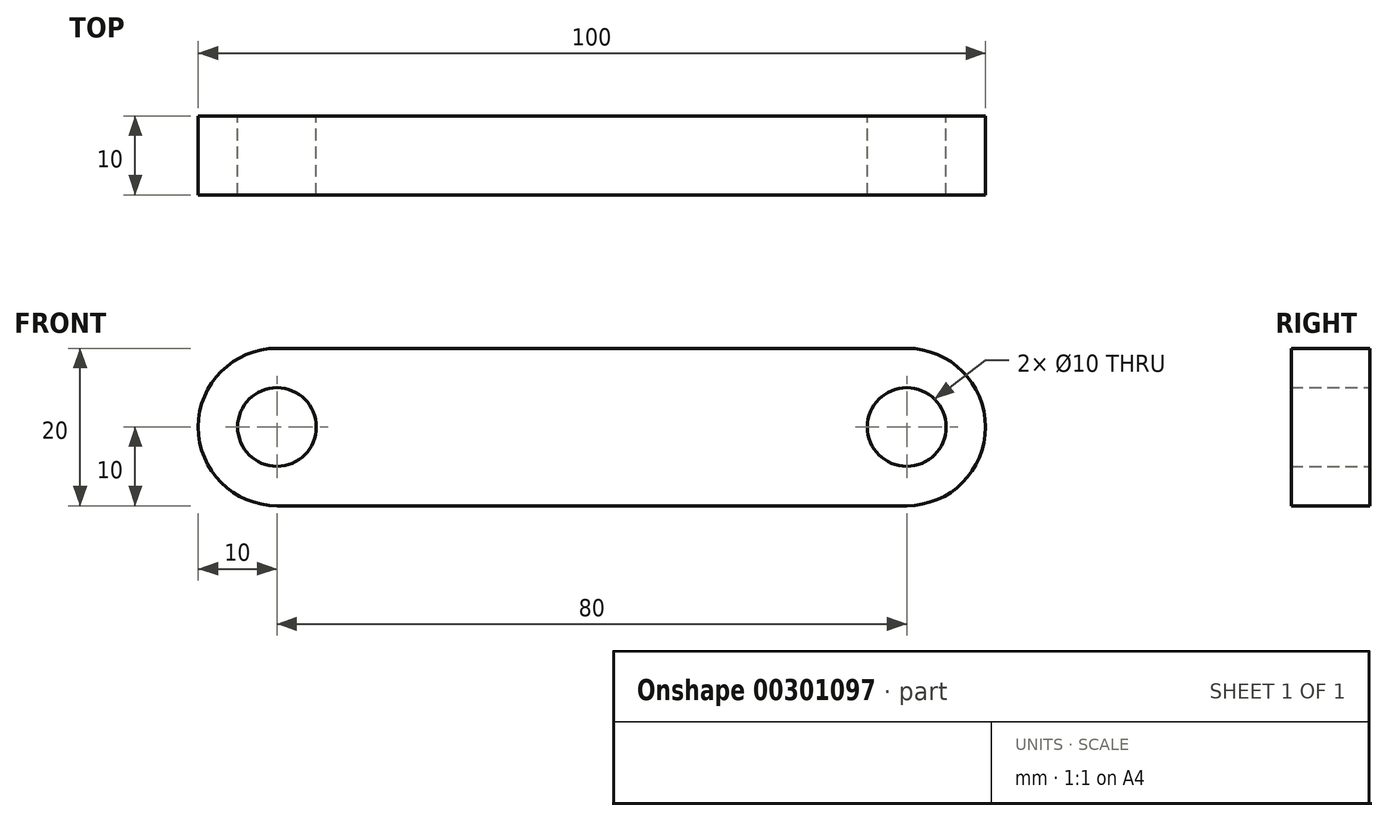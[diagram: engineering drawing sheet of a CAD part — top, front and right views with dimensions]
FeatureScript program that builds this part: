
annotation { "Feature Type Name" : "Feature", "Feature Type Description" : "" }
export const myFeature = defineFeature(function(context is Context, id is Id, definition is map)
    precondition{}
    {
        {
            var Q0;
            Q0=qCreatedBy(makeId("Front.planeOp"),FACE);
            var sketch = newSketch(context, id + "F0", { "sketchPlane" : qUnion([Q0])});
            skCircle(sketch, "E0", {"center": v(0, 0) * mm, "radius": 5 * mm});
            skCircle(sketch, "E1", {"center": v(80, 0) * mm, "radius": 5 * mm});
            skArc(sketch, "E2", {"start": v(0, 10) * mm, "mid": v(-10, 0) * mm, "end": v(0, -10) * mm});
            skArc(sketch, "E3", {"start": v(80, 10) * mm, "mid": v(90, 0) * mm, "end": v(80, -10) * mm});
            skLineSegment(sketch, "E4", {"start": v(0, 10) * mm, "end": v(80, 10) * mm});
            skLineSegment(sketch, "E5", {"start": v(0, -10) * mm, "end": v(80, -10) * mm});
            skSolve(sketch);
        }
        {
            var Q0;
            Q0 = qSketchRegion(id + "F0", true);
            extrude(context, id + "F1", {"entities" : qUnion([Q0]), "depth" : 10 * mm});
        }
    });
